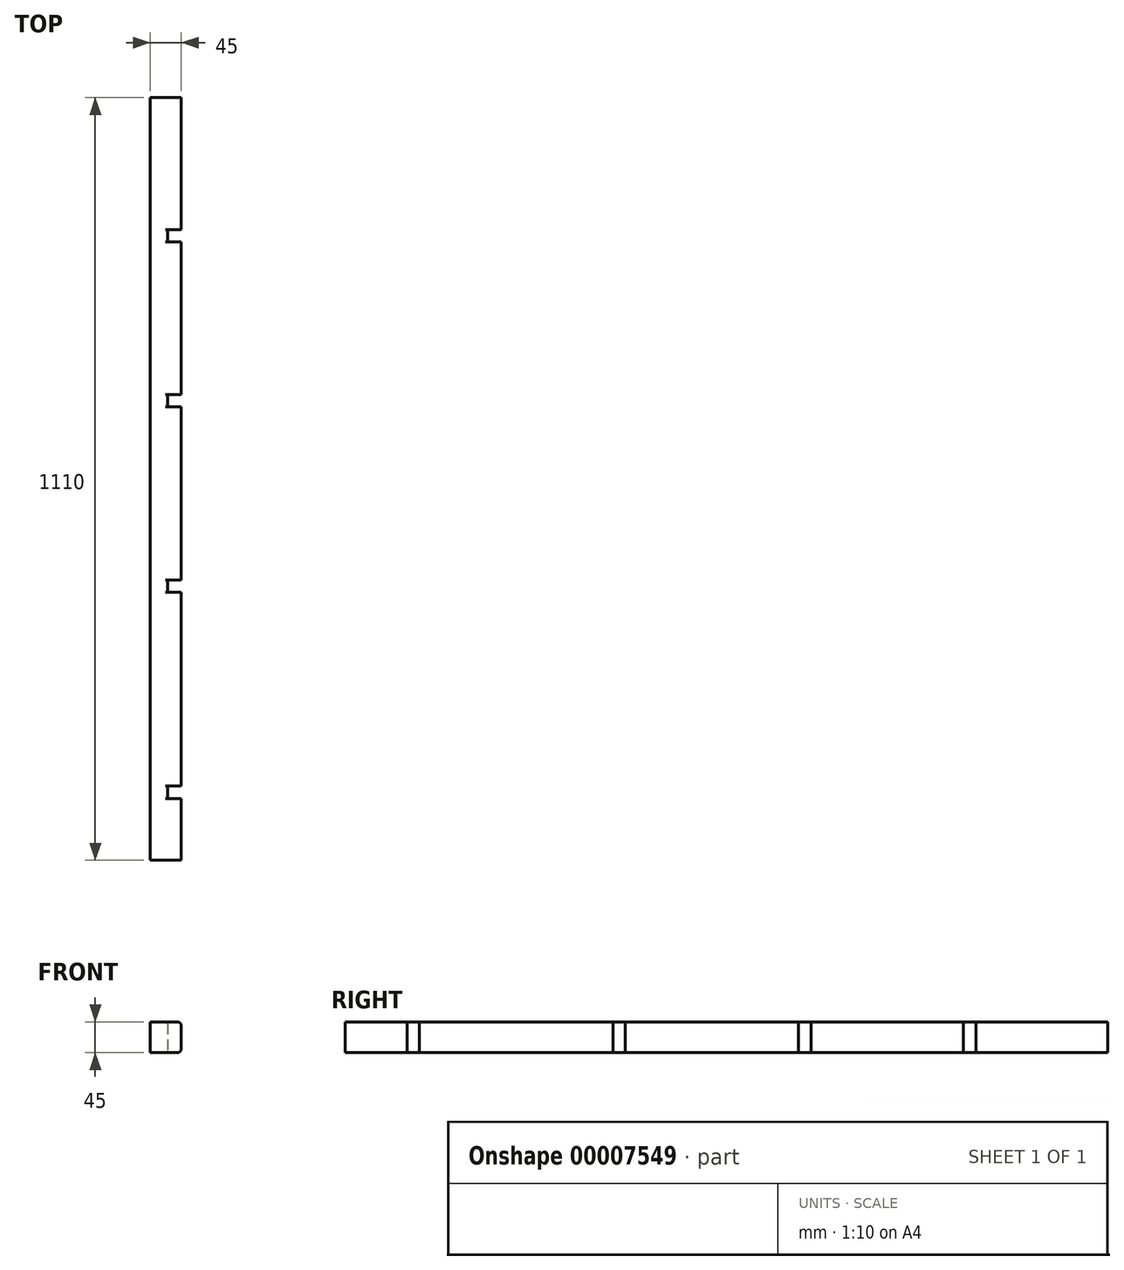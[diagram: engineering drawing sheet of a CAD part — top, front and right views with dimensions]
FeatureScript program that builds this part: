
annotation { "Feature Type Name" : "Feature", "Feature Type Description" : "" }
export const myFeature = defineFeature(function(context is Context, id is Id, definition is map)
    precondition{}
    {
        {
            var Q0;
            Q0=qCreatedBy(makeId("Top.planeOp"),FACE);
            var sketch = newSketch(context, id + "F0", { "sketchPlane" : qUnion([Q0])});
            skLineSegment(sketch, "E0", {"start": v(-675, 2240) * mm, "end": v(-675, -1510) * mm, "construction": true});
            skLineSegment(sketch, "E1", {"start": v(-675, -1510) * mm, "end": v(675, -1510) * mm, "construction": true});
            skLineSegment(sketch, "E2", {"start": v(675, -1510) * mm, "end": v(675, 2240) * mm, "construction": true});
            skLineSegment(sketch, "E3", {"start": v(675, 2240) * mm, "end": v(-675, 2240) * mm, "construction": true});
            skLineSegment(sketch, "E4.left", {"start": v(-675, 590) * mm, "end": v(-675, 110) * mm});
            skLineSegment(sketch, "E4.right", {"start": v(675, 590) * mm, "end": v(675, 110) * mm});
            skLineSegment(sketch, "E5", {"start": v(-675, 1990) * mm, "end": v(-675, 1510) * mm});
            skLineSegment(sketch, "E6", {"start": v(675, 1290) * mm, "end": v(675, 810) * mm});
            skLineSegment(sketch, "E7", {"start": v(-675, -590) * mm, "end": v(-675, -110) * mm});
            skLineSegment(sketch, "E8", {"start": v(-675, -810) * mm, "end": v(-675, -1310) * mm});
            skLineSegment(sketch, "E9", {"start": v(675, 1990) * mm, "end": v(675, 1510) * mm});
            skLineSegment(sketch, "E10", {"start": v(-420, 2240) * mm, "end": v(-420, -1510) * mm, "construction": true});
            skLineSegment(sketch, "E11", {"start": v(420, 2240) * mm, "end": v(420, -1510) * mm, "construction": true});
            skArc(sketch, "E12", {"start": v(-420, 1510) * mm, "mid": v(-403.52, 1507.7) * mm, "end": v(-388.3, 1500.94) * mm});
            skArc(sketch, "E13", {"start": v(-388.3, 1500.94) * mm, "mid": v(0, 1390) * mm, "end": v(388.3, 1500.94) * mm});
            skArc(sketch, "E14", {"start": v(388.3, 1500.94) * mm, "mid": v(403.52, 1507.7) * mm, "end": v(420, 1510) * mm});
            skLineSegment(sketch, "E15", {"start": v(-675, 1510) * mm, "end": v(-465, 1510) * mm});
            skLineSegment(sketch, "E16", {"start": v(-465, 1510) * mm, "end": v(-465, 1529) * mm});
            skLineSegment(sketch, "E17", {"start": v(-462, 1532) * mm, "end": v(-423, 1532) * mm});
            skLineSegment(sketch, "E18", {"start": v(-420, 1529) * mm, "end": v(-420, 1510) * mm});
            skLineSegment(sketch, "E19", {"start": v(-465, 1510) * mm, "end": v(-420, 1510) * mm, "construction": true});
            skLineSegment(sketch, "E20", {"start": v(-465, 2240) * mm, "end": v(-465, -1510) * mm, "construction": true});
            skLineSegment(sketch, "E21", {"start": v(465, 2240) * mm, "end": v(465, -1510) * mm, "construction": true});
            skLineSegment(sketch, "E22", {"start": v(0, -1510) * mm, "end": v(0, 2240) * mm, "construction": true});
            skLineSegment(sketch, "E23", {"start": v(-420, 810) * mm, "end": v(-420, 832) * mm});
            skLineSegment(sketch, "E24", {"start": v(-465, 832) * mm, "end": v(-465, 810) * mm});
            skLineSegment(sketch, "E25", {"start": v(-465, 810) * mm, "end": v(-675, 810) * mm});
            skLineSegment(sketch, "E26", {"start": v(-675, 810) * mm, "end": v(-675, 1290) * mm});
            skLineSegment(sketch, "E27", {"start": v(675, 810) * mm, "end": v(465, 810) * mm});
            skLineSegment(sketch, "E28", {"start": v(465, 810) * mm, "end": v(465, 832) * mm});
            skLineSegment(sketch, "E29", {"start": v(465, 832) * mm, "end": v(420, 832) * mm});
            skLineSegment(sketch, "E30", {"start": v(420, 832) * mm, "end": v(420, 810) * mm});
            skLineSegment(sketch, "E31", {"start": v(420, 1510) * mm, "end": v(420, 1529) * mm});
            skLineSegment(sketch, "E32", {"start": v(423, 1532) * mm, "end": v(462, 1532) * mm});
            skLineSegment(sketch, "E33", {"start": v(465, 1529) * mm, "end": v(465, 1510) * mm});
            skLineSegment(sketch, "E34", {"start": v(465, 1510) * mm, "end": v(675, 1510) * mm});
            skLineSegment(sketch, "E35", {"start": v(420, 1510) * mm, "end": v(465, 1510) * mm, "construction": true});
            skLineSegment(sketch, "E36", {"start": v(-200, 2240) * mm, "end": v(-200, -1510) * mm, "construction": true});
            skLineSegment(sketch, "E37", {"start": v(-245, 2240) * mm, "end": v(-245, -1510) * mm, "construction": true});
            skLineSegment(sketch, "E38", {"start": v(200, 2240) * mm, "end": v(200, -1510) * mm, "construction": true});
            skLineSegment(sketch, "E39", {"start": v(245, 2240) * mm, "end": v(245, -1510) * mm, "construction": true});
            skLineSegment(sketch, "E40", {"start": v(-675, 1990) * mm, "end": v(-245, 1990) * mm});
            skLineSegment(sketch, "E41", {"start": v(-245, 1990) * mm, "end": v(-245, 1971) * mm});
            skLineSegment(sketch, "E42", {"start": v(-242, 1968) * mm, "end": v(-203, 1968) * mm});
            skLineSegment(sketch, "E43", {"start": v(-200, 1971) * mm, "end": v(-200, 1990) * mm});
            skLineSegment(sketch, "E44", {"start": v(-200, 1990) * mm, "end": v(200, 1990) * mm});
            skLineSegment(sketch, "E45", {"start": v(200, 1990) * mm, "end": v(200, 1971) * mm});
            skLineSegment(sketch, "E46", {"start": v(203, 1968) * mm, "end": v(242, 1968) * mm});
            skLineSegment(sketch, "E47", {"start": v(245, 1971) * mm, "end": v(245, 1990) * mm});
            skLineSegment(sketch, "E48", {"start": v(245, 1990) * mm, "end": v(675, 1990) * mm});
            skLineSegment(sketch, "E49", {"start": v(-675, 1290) * mm, "end": v(-245, 1290) * mm});
            skLineSegment(sketch, "E50", {"start": v(-245, 1290) * mm, "end": v(-245, 1268) * mm});
            skLineSegment(sketch, "E51", {"start": v(-245, 1268) * mm, "end": v(-200, 1268) * mm});
            skLineSegment(sketch, "E52", {"start": v(-200, 1268) * mm, "end": v(-200, 1290) * mm});
            skLineSegment(sketch, "E53", {"start": v(-200, 1290) * mm, "end": v(200, 1290) * mm});
            skLineSegment(sketch, "E54", {"start": v(200, 1290) * mm, "end": v(200, 1268) * mm});
            skLineSegment(sketch, "E55", {"start": v(200, 1268) * mm, "end": v(245, 1268) * mm});
            skLineSegment(sketch, "E56", {"start": v(245, 1268) * mm, "end": v(245, 1290) * mm});
            skLineSegment(sketch, "E57", {"start": v(245, 1290) * mm, "end": v(675, 1290) * mm});
            skLineSegment(sketch, "E58", {"start": v(-465, 832) * mm, "end": v(-420, 832) * mm});
            skLineSegment(sketch, "E59", {"start": v(-420, 810) * mm, "end": v(-465, 810) * mm, "construction": true});
            skLineSegment(sketch, "E60", {"start": v(420, 810) * mm, "end": v(465, 810) * mm, "construction": true});
            skArc(sketch, "E61", {"start": v(-403.2, 807.6) * mm, "mid": v(0, 750) * mm, "end": v(403.2, 807.6) * mm});
            skArc(sketch, "E62", {"start": v(403.2, 807.6) * mm, "mid": v(411.51, 809.4) * mm, "end": v(420, 810) * mm});
            skArc(sketch, "E63", {"start": v(-403.2, 807.6) * mm, "mid": v(-411.51, 809.4) * mm, "end": v(-420, 810) * mm});
            skLineSegment(sketch, "E64", {"start": v(-675, 590) * mm, "end": v(-245, 590) * mm});
            skLineSegment(sketch, "E65", {"start": v(-245, 590) * mm, "end": v(-245, 568) * mm});
            skLineSegment(sketch, "E66", {"start": v(-245, 568) * mm, "end": v(-200, 568) * mm});
            skLineSegment(sketch, "E67", {"start": v(-200, 568) * mm, "end": v(-200, 590) * mm});
            skLineSegment(sketch, "E68", {"start": v(-200, 590) * mm, "end": v(200, 590) * mm});
            skLineSegment(sketch, "E69", {"start": v(200, 590) * mm, "end": v(200, 568) * mm});
            skLineSegment(sketch, "E70", {"start": v(200, 568) * mm, "end": v(245, 568) * mm});
            skLineSegment(sketch, "E71", {"start": v(245, 568) * mm, "end": v(245, 590) * mm});
            skLineSegment(sketch, "E72", {"start": v(245, 590) * mm, "end": v(675, 590) * mm});
            skLineSegment(sketch, "E73", {"start": v(675, 110) * mm, "end": v(465, 110) * mm});
            skLineSegment(sketch, "E74", {"start": v(465, 110) * mm, "end": v(465, 132) * mm});
            skLineSegment(sketch, "E75", {"start": v(465, 132) * mm, "end": v(420, 132) * mm});
            skLineSegment(sketch, "E76", {"start": v(420, 132) * mm, "end": v(420, 110) * mm});
            skLineSegment(sketch, "E77", {"start": v(-675, 110) * mm, "end": v(-465, 110) * mm});
            skLineSegment(sketch, "E78", {"start": v(-465, 110) * mm, "end": v(-465, 132) * mm});
            skLineSegment(sketch, "E79", {"start": v(-465, 132) * mm, "end": v(-420, 132) * mm});
            skLineSegment(sketch, "E80", {"start": v(-420, 132) * mm, "end": v(-420, 110) * mm});
            skLineSegment(sketch, "E81", {"start": v(-420, 110) * mm, "end": v(420, 110) * mm});
            skLineSegment(sketch, "E82", {"start": v(-675, -110) * mm, "end": v(-245, -110) * mm});
            skLineSegment(sketch, "E83", {"start": v(-245, -110) * mm, "end": v(-245, -132) * mm});
            skLineSegment(sketch, "E84", {"start": v(-245, -132) * mm, "end": v(-200, -132) * mm});
            skLineSegment(sketch, "E85", {"start": v(-200, -132) * mm, "end": v(-200, -110) * mm});
            skLineSegment(sketch, "E86", {"start": v(-200, -110) * mm, "end": v(200, -110) * mm});
            skLineSegment(sketch, "E87", {"start": v(200, -110) * mm, "end": v(200, -132) * mm});
            skLineSegment(sketch, "E88", {"start": v(200, -132) * mm, "end": v(245, -132) * mm});
            skLineSegment(sketch, "E89", {"start": v(245, -132) * mm, "end": v(245, -110) * mm});
            skLineSegment(sketch, "E90", {"start": v(245, -110) * mm, "end": v(675, -110) * mm});
            skLineSegment(sketch, "E91", {"start": v(675, -110) * mm, "end": v(675, -590) * mm});
            skLineSegment(sketch, "E92", {"start": v(675, -590) * mm, "end": v(465, -590) * mm});
            skLineSegment(sketch, "E93", {"start": v(465, -590) * mm, "end": v(465, -568) * mm});
            skLineSegment(sketch, "E94", {"start": v(465, -568) * mm, "end": v(420, -568) * mm});
            skLineSegment(sketch, "E95", {"start": v(420, -568) * mm, "end": v(420, -590) * mm});
            skLineSegment(sketch, "E96", {"start": v(420, -590) * mm, "end": v(465, -590) * mm, "construction": true});
            skLineSegment(sketch, "E97", {"start": v(-675, -590) * mm, "end": v(-465, -590) * mm});
            skLineSegment(sketch, "E98", {"start": v(-465, -590) * mm, "end": v(-465, -568) * mm});
            skLineSegment(sketch, "E99", {"start": v(-465, -568) * mm, "end": v(-420, -568) * mm});
            skLineSegment(sketch, "E100", {"start": v(-420, -568) * mm, "end": v(-420, -590) * mm});
            skLineSegment(sketch, "E101", {"start": v(-420, -590) * mm, "end": v(-465, -590) * mm, "construction": true});
            skArc(sketch, "E102", {"start": v(-403.2, -587.6) * mm, "mid": v(0, -530) * mm, "end": v(403.2, -587.6) * mm});
            skArc(sketch, "E103", {"start": v(403.2, -587.6) * mm, "mid": v(411.51, -589.4) * mm, "end": v(420, -590) * mm});
            skArc(sketch, "E104", {"start": v(-403.2, -587.6) * mm, "mid": v(-411.51, -589.4) * mm, "end": v(-420, -590) * mm});
            skLineSegment(sketch, "E105", {"start": v(-465, -1310) * mm, "end": v(-420, -1310) * mm, "construction": true});
            skLineSegment(sketch, "E106", {"start": v(-420, -1310) * mm, "end": v(-420, -1310) * mm});
            skLineSegment(sketch, "E107", {"start": v(-420, -1310) * mm, "end": v(-465, -1310) * mm});
            skLineSegment(sketch, "E108", {"start": v(-465, -1310) * mm, "end": v(-465, -1310) * mm});
            skLineSegment(sketch, "E109", {"start": v(-465, -1310) * mm, "end": v(-675, -1310) * mm});
            skLineSegment(sketch, "E110", {"start": v(-675, -810) * mm, "end": v(-245, -810) * mm});
            skLineSegment(sketch, "E111", {"start": v(-245, -810) * mm, "end": v(-245, -810) * mm});
            skLineSegment(sketch, "E112", {"start": v(-245, -810) * mm, "end": v(-200, -810) * mm});
            skLineSegment(sketch, "E113", {"start": v(-200, -810) * mm, "end": v(-200, -810) * mm});
            skLineSegment(sketch, "E114", {"start": v(-200, -810) * mm, "end": v(200, -810) * mm});
            skLineSegment(sketch, "E115", {"start": v(200, -810) * mm, "end": v(200, -810) * mm});
            skLineSegment(sketch, "E116", {"start": v(200, -810) * mm, "end": v(245, -810) * mm});
            skLineSegment(sketch, "E117", {"start": v(245, -810) * mm, "end": v(245, -810) * mm});
            skLineSegment(sketch, "E118", {"start": v(245, -810) * mm, "end": v(675, -810) * mm});
            skLineSegment(sketch, "E119", {"start": v(675, -810) * mm, "end": v(675, -1310) * mm});
            skLineSegment(sketch, "E120", {"start": v(675, -1310) * mm, "end": v(465, -1310) * mm});
            skLineSegment(sketch, "E121", {"start": v(465, -1310) * mm, "end": v(465, -1310) * mm});
            skLineSegment(sketch, "E122", {"start": v(465, -1310) * mm, "end": v(420, -1310) * mm});
            skLineSegment(sketch, "E123", {"start": v(420, -1310) * mm, "end": v(420, -1310) * mm});
            skLineSegment(sketch, "E124", {"start": v(420, -1310) * mm, "end": v(465, -1310) * mm, "construction": true});
            skArc(sketch, "E125", {"start": v(420, -1310) * mm, "mid": v(403.52, -1307.7) * mm, "end": v(388.3, -1300.94) * mm});
            skArc(sketch, "E126", {"start": v(388.3, -1300.94) * mm, "mid": v(0, -1190) * mm, "end": v(-388.3, -1300.94) * mm});
            skArc(sketch, "E127", {"start": v(-388.3, -1300.94) * mm, "mid": v(-403.52, -1307.7) * mm, "end": v(-420, -1310) * mm});
            skPoint(sketch, "E128.visualSharp", {"position": v(-465, 1532) * mm});
            skArc(sketch, "E128.filletArc", {"start": v(-462, 1532) * mm, "mid": v(-464.12, 1531.12) * mm, "end": v(-465, 1529) * mm});
            skPoint(sketch, "E129.visualSharp", {"position": v(-420, 1532) * mm});
            skArc(sketch, "E129.filletArc", {"start": v(-420, 1529) * mm, "mid": v(-420.88, 1531.12) * mm, "end": v(-423, 1532) * mm});
            skPoint(sketch, "E130.visualSharp", {"position": v(-245, 1968) * mm});
            skArc(sketch, "E130.filletArc", {"start": v(-245, 1971) * mm, "mid": v(-244.12, 1968.88) * mm, "end": v(-242, 1968) * mm});
            skPoint(sketch, "E131.visualSharp", {"position": v(-200, 1968) * mm});
            skArc(sketch, "E131.filletArc", {"start": v(-203, 1968) * mm, "mid": v(-200.88, 1968.88) * mm, "end": v(-200, 1971) * mm});
            skPoint(sketch, "E132.visualSharp", {"position": v(200, 1968) * mm});
            skArc(sketch, "E132.filletArc", {"start": v(200, 1971) * mm, "mid": v(200.88, 1968.88) * mm, "end": v(203, 1968) * mm});
            skPoint(sketch, "E133.visualSharp", {"position": v(245, 1968) * mm});
            skArc(sketch, "E133.filletArc", {"start": v(242, 1968) * mm, "mid": v(244.12, 1968.88) * mm, "end": v(245, 1971) * mm});
            skPoint(sketch, "E134.visualSharp", {"position": v(420, 1532) * mm});
            skArc(sketch, "E134.filletArc", {"start": v(423, 1532) * mm, "mid": v(420.88, 1531.12) * mm, "end": v(420, 1529) * mm});
            skPoint(sketch, "E135.visualSharp", {"position": v(465, 1532) * mm});
            skArc(sketch, "E135.filletArc", {"start": v(465, 1529) * mm, "mid": v(464.12, 1531.12) * mm, "end": v(462, 1532) * mm});
            skSolve(sketch);
        }
        {
            var Q0;
            Q0 = qSketchRegion(id + "F0", true);
            extrude(context, id + "F1", {"entities" : qUnion([Q0]), "depth" : 18 * mm});
        }
        {
            var Q0;
            Q0=qCreatedBy(makeId("Top.planeOp"),FACE);
            var sketch = newSketch(context, id + "F2", { "sketchPlane" : qUnion([Q0])});
            skLineSegment(sketch, "E136", {"start": v(884.05, 1110) * mm, "end": v(884.05, 0) * mm});
            skLineSegment(sketch, "E137", {"start": v(884.05, 0) * mm, "end": v(929.05, 0) * mm});
            skLineSegment(sketch, "E138", {"start": v(929.05, 0) * mm, "end": v(929.05, 90) * mm});
            skLineSegment(sketch, "E139", {"start": v(929.05, 90) * mm, "end": v(909.05, 90) * mm});
            skLineSegment(sketch, "E140", {"start": v(909.05, 90) * mm, "end": v(909.05, 108) * mm});
            skLineSegment(sketch, "E141", {"start": v(909.05, 108) * mm, "end": v(929.05, 108) * mm});
            skLineSegment(sketch, "E142", {"start": v(929.05, 108) * mm, "end": v(929.05, 390) * mm});
            skLineSegment(sketch, "E143", {"start": v(929.05, 390) * mm, "end": v(909.05, 390) * mm});
            skLineSegment(sketch, "E144", {"start": v(909.05, 390) * mm, "end": v(909.05, 408) * mm});
            skLineSegment(sketch, "E145", {"start": v(909.05, 408) * mm, "end": v(929.05, 408) * mm});
            skLineSegment(sketch, "E146", {"start": v(929.05, 408) * mm, "end": v(929.05, 660) * mm});
            skLineSegment(sketch, "E147", {"start": v(929.05, 660) * mm, "end": v(909.05, 660) * mm});
            skLineSegment(sketch, "E148", {"start": v(909.05, 660) * mm, "end": v(909.05, 678) * mm});
            skLineSegment(sketch, "E149", {"start": v(909.05, 678) * mm, "end": v(929.05, 678) * mm});
            skLineSegment(sketch, "E150", {"start": v(929.05, 678) * mm, "end": v(929.05, 900) * mm});
            skLineSegment(sketch, "E151", {"start": v(929.05, 900) * mm, "end": v(909.05, 900) * mm});
            skLineSegment(sketch, "E152", {"start": v(909.05, 900) * mm, "end": v(909.05, 918) * mm});
            skLineSegment(sketch, "E153", {"start": v(909.05, 918) * mm, "end": v(929.05, 918) * mm});
            skLineSegment(sketch, "E154", {"start": v(929.05, 918) * mm, "end": v(929.05, 1110) * mm});
            skLineSegment(sketch, "E155", {"start": v(929.05, 1110) * mm, "end": v(884.05, 1110) * mm});
            skLineSegment(sketch, "E156.bottom", {"start": v(1362.14, 0) * mm, "end": v(1842.14, 0) * mm});
            skLineSegment(sketch, "E156.top", {"start": v(1362.14, 1150) * mm, "end": v(1842.14, 1150) * mm});
            skLineSegment(sketch, "E156.left", {"start": v(1362.14, 0) * mm, "end": v(1362.14, 1150) * mm});
            skLineSegment(sketch, "E156.right", {"start": v(1842.14, 0) * mm, "end": v(1842.14, 1150) * mm});
            skLineSegment(sketch, "E157", {"start": v(909.05, 909) * mm, "end": v(1842.14, 909) * mm, "construction": true});
            skLineSegment(sketch, "E158", {"start": v(909.05, 669) * mm, "end": v(1842.14, 669) * mm, "construction": true});
            skLineSegment(sketch, "E159", {"start": v(909.05, 399) * mm, "end": v(1842.14, 399) * mm, "construction": true});
            skLineSegment(sketch, "E160", {"start": v(909.05, 99) * mm, "end": v(1842.14, 99) * mm, "construction": true});
            skLineSegment(sketch, "E161", {"start": v(1602.14, 1150) * mm, "end": v(1602.14, 0) * mm, "construction": true});
            skLineSegment(sketch, "E162", {"start": v(1402.14, 1150) * mm, "end": v(1402.14, 0) * mm, "construction": true});
            skLineSegment(sketch, "E163", {"start": v(1802.14, 1150) * mm, "end": v(1802.14, 0) * mm, "construction": true});
            skCircle(sketch, "E164", {"center": v(1402.14, 909) * mm, "radius": 3 * mm});
            skCircle(sketch, "E165", {"center": v(1402.14, 669) * mm, "radius": 3 * mm});
            skCircle(sketch, "E166", {"center": v(1402.14, 399) * mm, "radius": 3 * mm});
            skCircle(sketch, "E167", {"center": v(1402.14, 99) * mm, "radius": 3 * mm});
            skLineSegment(sketch, "E168.direction1", {"start": v(1402.14, 909) * mm, "end": v(1602.14, 909) * mm, "construction": true});
            skLineSegment(sketch, "E169", {"start": v(884.05, 1119) * mm, "end": v(1842.14, 1119) * mm, "construction": true});
            skCircle(sketch, "E170", {"center": v(1402.14, 1119) * mm, "radius": 3 * mm});
            skCircle(sketch, "E171.1.0.0", {"center": v(1502.14, 669) * mm, "radius": 3 * mm});
            skCircle(sketch, "E171.1.0.1", {"center": v(1502.14, 909) * mm, "radius": 3 * mm});
            skCircle(sketch, "E171.1.0.2", {"center": v(1502.14, 399) * mm, "radius": 3 * mm});
            skCircle(sketch, "E171.1.0.3", {"center": v(1502.14, 1119) * mm, "radius": 3 * mm});
            skCircle(sketch, "E171.1.0.4", {"center": v(1502.14, 99) * mm, "radius": 3 * mm});
            skCircle(sketch, "E171.2.0.0", {"center": v(1602.14, 669) * mm, "radius": 3 * mm});
            skCircle(sketch, "E171.2.0.1", {"center": v(1602.14, 909) * mm, "radius": 3 * mm});
            skCircle(sketch, "E171.2.0.2", {"center": v(1602.14, 399) * mm, "radius": 3 * mm});
            skCircle(sketch, "E171.2.0.3", {"center": v(1602.14, 1119) * mm, "radius": 3 * mm});
            skCircle(sketch, "E171.2.0.4", {"center": v(1602.14, 99) * mm, "radius": 3 * mm});
            skLineSegment(sketch, "E171.direction1", {"start": v(1402.14, 669) * mm, "end": v(1502.14, 669) * mm, "construction": true});
            skCircle(sketch, "E172.0.3.0", {"center": v(1702.14, 669) * mm, "radius": 3 * mm});
            skCircle(sketch, "E172.2.3.0", {"center": v(1702.14, 909) * mm, "radius": 3 * mm});
            skCircle(sketch, "E172.4.3.0", {"center": v(1702.14, 399) * mm, "radius": 3 * mm});
            skCircle(sketch, "E172.6.3.0", {"center": v(1702.14, 1119) * mm, "radius": 3 * mm});
            skCircle(sketch, "E172.8.3.0", {"center": v(1702.14, 99) * mm, "radius": 3 * mm});
            skCircle(sketch, "E172.0.4.0", {"center": v(1802.14, 669) * mm, "radius": 3 * mm});
            skCircle(sketch, "E172.2.4.0", {"center": v(1802.14, 909) * mm, "radius": 3 * mm});
            skCircle(sketch, "E172.4.4.0", {"center": v(1802.14, 399) * mm, "radius": 3 * mm});
            skCircle(sketch, "E172.6.4.0", {"center": v(1802.14, 1119) * mm, "radius": 3 * mm});
            skCircle(sketch, "E172.8.4.0", {"center": v(1802.14, 99) * mm, "radius": 3 * mm});
            skSolve(sketch);
        }
        {
            var Q0;
            Q0=makeQuery(id+"F2.imprint","IMPRINT",FACE,{"disambiguationData":[TD([[makeQuery(id+"F2.imprint","IMPRINT",EDGE,{"derivedFrom":sQuery(id+"F2.wireOp",EDGE,"E136")}),1.0]])]});
            extrude(context, id + "F3", {"entities" : qUnion([Q0]), "depth" : 45 * mm});
        }
        {
            var Q0;
            Q0=makeQuery(id+"F2.imprint","IMPRINT",FACE,{"disambiguationData":[TD([[makeQuery(id+"F2.imprint","IMPRINT",EDGE,{"derivedFrom":sQuery(id+"F2.wireOp",EDGE,"E156.bottom")}),1.0]])]});
            extrude(context, id + "F4", {"entities" : qUnion([Q0]), "depth" : 18 * mm});
        }
        {
            var Q0;
            Q0=makeQuery(id+"F4.opExtrude","CAP_EDGE",EDGE,{"disambiguationData":[OSD([sQuery(id+"F2.wireOp",EDGE,"E170")])],"isStart":false});
            var Q1;
            Q1=makeQuery(id+"F4.opExtrude","CAP_EDGE",EDGE,{"disambiguationData":[OSD([sQuery(id+"F2.wireOp",EDGE,"E171.2.0.3")])],"isStart":false});
            var Q2;
            Q2=makeQuery(id+"F4.opExtrude","CAP_EDGE",EDGE,{"disambiguationData":[OSD([sQuery(id+"F2.wireOp",EDGE,"E164")])],"isStart":false});
            var Q3;
            Q3=makeQuery(id+"F4.opExtrude","CAP_EDGE",EDGE,{"disambiguationData":[OSD([sQuery(id+"F2.wireOp",EDGE,"E171.2.0.1")])],"isStart":false});
            var Q4;
            Q4=makeQuery(id+"F4.opExtrude","CAP_EDGE",EDGE,{"disambiguationData":[OSD([sQuery(id+"F2.wireOp",EDGE,"E165")])],"isStart":false});
            var Q5;
            Q5=makeQuery(id+"F4.opExtrude","CAP_EDGE",EDGE,{"disambiguationData":[OSD([sQuery(id+"F2.wireOp",EDGE,"E171.2.0.0")])],"isStart":false});
            var Q6;
            Q6=makeQuery(id+"F4.opExtrude","CAP_EDGE",EDGE,{"disambiguationData":[OSD([sQuery(id+"F2.wireOp",EDGE,"E166")])],"isStart":false});
            var Q7;
            Q7=makeQuery(id+"F4.opExtrude","CAP_EDGE",EDGE,{"disambiguationData":[OSD([sQuery(id+"F2.wireOp",EDGE,"E171.2.0.2")])],"isStart":false});
            var Q8;
            Q8=makeQuery(id+"F4.opExtrude","CAP_EDGE",EDGE,{"disambiguationData":[OSD([sQuery(id+"F2.wireOp",EDGE,"E167")])],"isStart":false});
            var Q9;
            Q9=makeQuery(id+"F4.opExtrude","CAP_EDGE",EDGE,{"disambiguationData":[OSD([sQuery(id+"F2.wireOp",EDGE,"E171.2.0.4")])],"isStart":false});
            var Q10;
            Q10=makeQuery(id+"F4.opExtrude","CAP_EDGE",EDGE,{"disambiguationData":[OSD([sQuery(id+"F2.wireOp",EDGE,"E172.6.4.0")])],"isStart":false});
            var Q11;
            Q11=makeQuery(id+"F4.opExtrude","CAP_EDGE",EDGE,{"disambiguationData":[OSD([sQuery(id+"F2.wireOp",EDGE,"E172.2.4.0")])],"isStart":false});
            var Q12;
            Q12=makeQuery(id+"F4.opExtrude","CAP_EDGE",EDGE,{"disambiguationData":[OSD([sQuery(id+"F2.wireOp",EDGE,"E172.0.4.0")])],"isStart":false});
            var Q13;
            Q13=makeQuery(id+"F4.opExtrude","CAP_EDGE",EDGE,{"disambiguationData":[OSD([sQuery(id+"F2.wireOp",EDGE,"E172.4.4.0")])],"isStart":false});
            var Q14;
            Q14=makeQuery(id+"F4.opExtrude","CAP_EDGE",EDGE,{"disambiguationData":[OSD([sQuery(id+"F2.wireOp",EDGE,"E172.8.4.0")])],"isStart":false});
            chamfer(context, id + "F5", {"entities" : qUnion([Q0, Q1, Q2, Q3, Q4, Q5, Q6, Q7, Q8, Q9, Q10, Q11, Q12, Q13, Q14]), "width" : 4 * mm});
        }
        {
            var Q0;
            Q0=makeQuery(id+"F4.opExtrude","SWEPT_FACE",FACE,{"disambiguationData":[OSD([sQuery(id+"F2.wireOp",EDGE,"E156.right")])]});
            var sketch = newSketch(context, id + "F6", { "sketchPlane" : qUnion([Q0])});
            skLineSegment(sketch, "E173.bottom", {"start": v(91, 0) * mm, "end": v(109, 0) * mm});
            skLineSegment(sketch, "E173.top", {"start": v(91, 6) * mm, "end": v(109, 6) * mm});
            skLineSegment(sketch, "E173.left", {"start": v(91, 0) * mm, "end": v(91, 6) * mm});
            skLineSegment(sketch, "E173.right", {"start": v(109, 0) * mm, "end": v(109, 6) * mm});
            skLineSegment(sketch, "E174.bottom", {"start": v(391, 0) * mm, "end": v(409, 0) * mm});
            skLineSegment(sketch, "E174.top", {"start": v(391, 6) * mm, "end": v(409, 6) * mm});
            skLineSegment(sketch, "E174.left", {"start": v(391, 0) * mm, "end": v(391, 6) * mm});
            skLineSegment(sketch, "E174.right", {"start": v(409, 0) * mm, "end": v(409, 6) * mm});
            skLineSegment(sketch, "E175.bottom", {"start": v(661, 0) * mm, "end": v(679, 0) * mm});
            skLineSegment(sketch, "E175.top", {"start": v(661, 6) * mm, "end": v(679, 6) * mm});
            skLineSegment(sketch, "E175.left", {"start": v(661, 0) * mm, "end": v(661, 6) * mm});
            skLineSegment(sketch, "E175.right", {"start": v(679, 0) * mm, "end": v(679, 6) * mm});
            skLineSegment(sketch, "E176.bottom", {"start": v(901, 0) * mm, "end": v(919, 0) * mm});
            skLineSegment(sketch, "E176.top", {"start": v(901, 6) * mm, "end": v(919, 6) * mm});
            skLineSegment(sketch, "E176.left", {"start": v(901, 0) * mm, "end": v(901, 6) * mm});
            skLineSegment(sketch, "E176.right", {"start": v(919, 0) * mm, "end": v(919, 6) * mm});
            skLineSegment(sketch, "E177.bottom", {"start": v(1111, 0) * mm, "end": v(1129, 0) * mm});
            skLineSegment(sketch, "E177.top", {"start": v(1111, 6) * mm, "end": v(1129, 6) * mm});
            skLineSegment(sketch, "E177.left", {"start": v(1111, 0) * mm, "end": v(1111, 6) * mm});
            skLineSegment(sketch, "E177.right", {"start": v(1129, 0) * mm, "end": v(1129, 6) * mm});
            skSolve(sketch);
        }
        {
            var Q0;
            Q0 = qSketchRegion(id + "F6", true);
            var Q1;
            Q1=makeQuery(id+"F4.opExtrude","SWEPT_FACE",FACE,{"disambiguationData":[OSD([sQuery(id+"F2.wireOp",EDGE,"E156.left")])]});
            extrude(context, id + "F7", {"entities" : qUnion([Q0]), "operationType" : NewBodyOperationType.REMOVE, "endBound" : BoundingType.UP_TO_SURFACE, "oppositeDirection" : true, "endBoundEntityFace" : qUnion([Q1]), "depth" : 25 * mm});
        }
        {
            var Q0;
            Q0=qCreatedBy(makeId("Top.planeOp"),FACE);
            var sketch = newSketch(context, id + "F8", { "sketchPlane" : qUnion([Q0])});
            skLineSegment(sketch, "E178.bottom", {"start": v(-593.1, -1424.37) * mm, "end": v(780.9, -1424.37) * mm});
            skLineSegment(sketch, "E178.top", {"start": v(-593.1, -1445.37) * mm, "end": v(780.9, -1445.37) * mm});
            skLineSegment(sketch, "E178.left", {"start": v(-593.1, -1424.37) * mm, "end": v(-593.1, -1445.37) * mm});
            skLineSegment(sketch, "E178.right", {"start": v(780.9, -1424.37) * mm, "end": v(780.9, -1445.37) * mm});
            skSolve(sketch);
        }
        {
            var Q0;
            Q0=makeQuery(id+"F8.imprint","IMPRINT",FACE,{"disambiguationData":[TD([[makeQuery(id+"F8.imprint","IMPRINT",EDGE,{"derivedFrom":sQuery(id+"F8.wireOp",EDGE,"E178.bottom")}),-1.0]])]});
            var Q1;
            Q1=sQuery(id+"F8.wireOp",EDGE,"E178.top");
            extrude(context, id + "F9", {"entities" : qUnion([Q0]), "surfaceEntities" : qUnion([Q1]), "depth" : 21 * mm});
        }
        {
            var Q0;
            Q0=makeQuery(id+"F3.opExtrude","SWEPT_FACE",FACE,{"disambiguationData":[OSD([sQuery(id+"F2.wireOp",EDGE,"E137")])]});
            var sketch = newSketch(context, id + "F10", { "sketchPlane" : qUnion([Q0])});
            skLineSegment(sketch, "E179", {"start": v(884.05, 45) * mm, "end": v(923.05, 45) * mm});
            skLineSegment(sketch, "E180", {"start": v(929.05, 39) * mm, "end": v(929.05, 6) * mm});
            skLineSegment(sketch, "E181", {"start": v(923.05, 0) * mm, "end": v(884.05, 0) * mm});
            skLineSegment(sketch, "E182", {"start": v(884.05, 0) * mm, "end": v(884.05, 45) * mm});
            skPoint(sketch, "E183.visualSharp", {"position": v(929.05, 45) * mm});
            skArc(sketch, "E183.filletArc", {"start": v(929.05, 39) * mm, "mid": v(927.3, 43.24) * mm, "end": v(923.05, 45) * mm});
            skPoint(sketch, "E184.visualSharp", {"position": v(929.05, 0) * mm});
            skArc(sketch, "E184.filletArc", {"start": v(923.05, 0) * mm, "mid": v(927.3, 1.76) * mm, "end": v(929.05, 6) * mm});
            skSolve(sketch);
        }
        {
            var Q0;
            Q0 = qSketchRegion(id + "F10", true);
            extrude(context, id + "F11", {"entities" : qUnion([Q0]), "operationType" : NewBodyOperationType.INTERSECT, "endBound" : BoundingType.THROUGH_ALL, "oppositeDirection" : true, "depth" : 25 * mm});
        }
        {
            var Q0;
            Q0=makeQuery(id+"F3.opExtrude","CAP_EDGE",EDGE,{"disambiguationData":[OSD([sQuery(id+"F2.wireOp",EDGE,"E140")])],"isStart":false});
            var Q1;
            Q1=makeQuery(id+"F3.opExtrude","CAP_EDGE",EDGE,{"disambiguationData":[OSD([sQuery(id+"F2.wireOp",EDGE,"E140")])],"isStart":true});
            var Q2;
            Q2=makeQuery(id+"F3.opExtrude","CAP_EDGE",EDGE,{"disambiguationData":[OSD([sQuery(id+"F2.wireOp",EDGE,"E144")])],"isStart":false});
            var Q3;
            Q3=makeQuery(id+"F3.opExtrude","CAP_EDGE",EDGE,{"disambiguationData":[OSD([sQuery(id+"F2.wireOp",EDGE,"E144")])],"isStart":true});
            var Q4;
            Q4=makeQuery(id+"F3.opExtrude","CAP_EDGE",EDGE,{"disambiguationData":[OSD([sQuery(id+"F2.wireOp",EDGE,"E148")])],"isStart":false});
            var Q5;
            Q5=makeQuery(id+"F3.opExtrude","CAP_EDGE",EDGE,{"disambiguationData":[OSD([sQuery(id+"F2.wireOp",EDGE,"E148")])],"isStart":true});
            var Q6;
            Q6=makeQuery(id+"F3.opExtrude","CAP_EDGE",EDGE,{"disambiguationData":[OSD([sQuery(id+"F2.wireOp",EDGE,"E152")])],"isStart":false});
            var Q7;
            Q7=makeQuery(id+"F3.opExtrude","CAP_EDGE",EDGE,{"disambiguationData":[OSD([sQuery(id+"F2.wireOp",EDGE,"E152")])],"isStart":true});
            fillet(context, id + "F12", {"entities" : qUnion([Q0, Q1, Q2, Q3, Q4, Q5, Q6, Q7]), "radius" : 3 * mm, "allowEdgeOverflow" : false});
        }
    });
